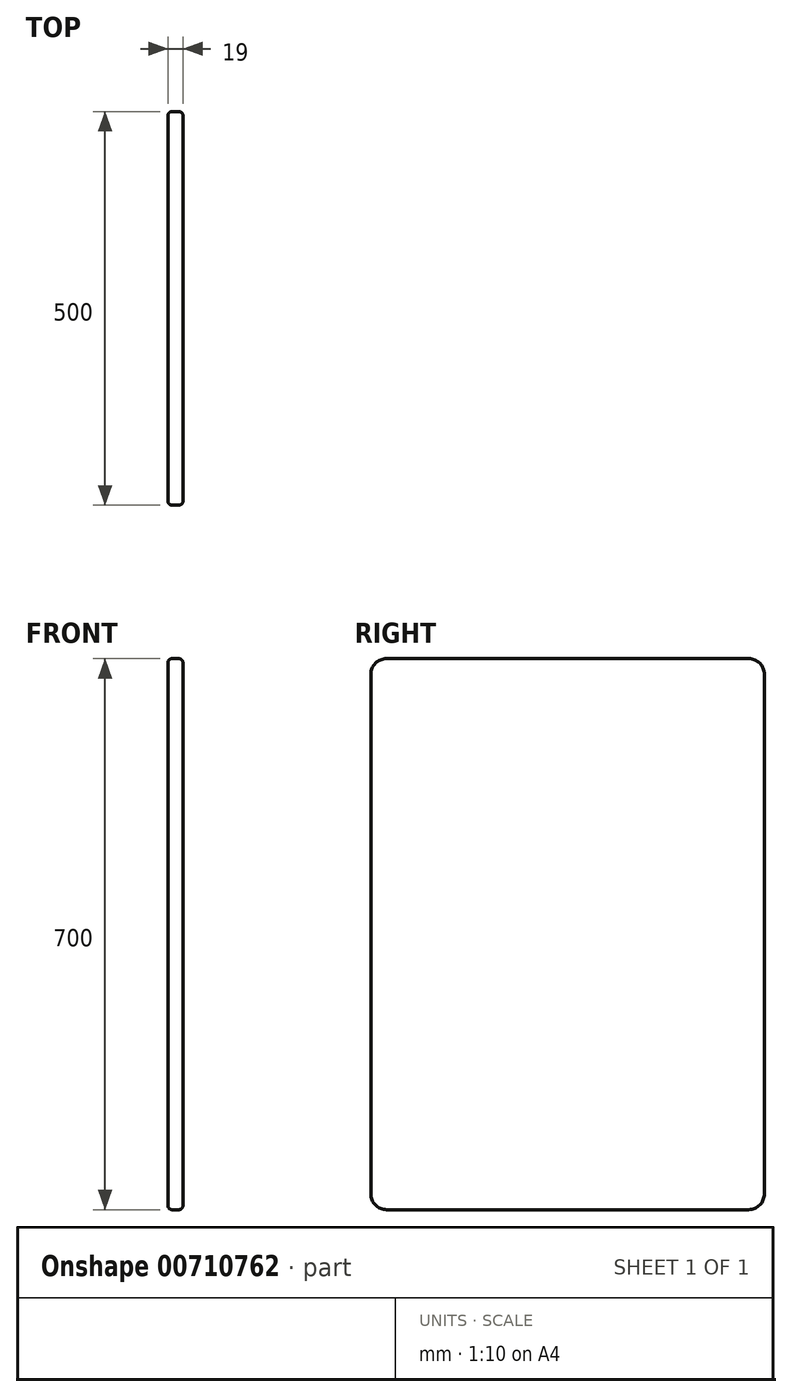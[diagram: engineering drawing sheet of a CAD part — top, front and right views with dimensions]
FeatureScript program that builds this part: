
annotation { "Feature Type Name" : "Feature", "Feature Type Description" : "" }
export const myFeature = defineFeature(function(context is Context, id is Id, definition is map)
    precondition{}
    {
        {
            var Q0;
            Q0=qCreatedBy(makeId("Right.planeOp"),FACE);
            var sketch = newSketch(context, id + "F0", { "sketchPlane" : qUnion([Q0])});
            skLineSegment(sketch, "E0.bottom", {"start": v(-33.4, 717.11) * mm, "end": v(466.6, 717.11) * mm});
            skLineSegment(sketch, "E0.top", {"start": v(-33.4, 17.11) * mm, "end": v(466.6, 17.11) * mm});
            skLineSegment(sketch, "E0.left", {"start": v(-33.4, 717.11) * mm, "end": v(-33.4, 17.11) * mm});
            skLineSegment(sketch, "E0.right", {"start": v(466.6, 717.11) * mm, "end": v(466.6, 17.11) * mm});
            skLineSegment(sketch, "E1", {"start": v(-33.4, 117.11) * mm, "end": v(466.6, 117.11) * mm, "construction": true});
            skLineSegment(sketch, "E2", {"start": v(-33.4, 367.11) * mm, "end": v(466.6, 367.11) * mm, "construction": true});
            skLineSegment(sketch, "E3", {"start": v(-33.4, 617.11) * mm, "end": v(466.6, 617.11) * mm, "construction": true});
            skSolve(sketch);
        }
        {
            var Q0;
            Q0=makeQuery(id+"F0.imprint","IMPRINT",FACE,{"disambiguationData":[TD([[makeQuery(id+"F0.imprint","IMPRINT",EDGE,{"derivedFrom":sQuery(id+"F0.wireOp",EDGE,"E0.bottom")}),-1.0]])]});
            extrude(context, id + "F1", {"entities" : qUnion([Q0]), "depth" : 19 * mm, "offsetDistance" : 25.4 * mm});
        }
        {
            var Q0;
            Q0=makeQuery(id+"F1.opExtrude","SWEPT_EDGE",EDGE,{"disambiguationData":[OSD([sQuery(id+"F0.wireOp",EDGE,"E0.bottom"),sQuery(id+"F0.wireOp",EDGE,"E0.left")])]});
            var Q1;
            Q1=makeQuery(id+"F1.opExtrude","SWEPT_EDGE",EDGE,{"disambiguationData":[OSD([sQuery(id+"F0.wireOp",EDGE,"E0.top"),sQuery(id+"F0.wireOp",EDGE,"E0.left")])]});
            var Q2;
            Q2=makeQuery(id+"F1.opExtrude","SWEPT_EDGE",EDGE,{"disambiguationData":[OSD([sQuery(id+"F0.wireOp",EDGE,"E0.top"),sQuery(id+"F0.wireOp",EDGE,"E0.right")])]});
            var Q3;
            Q3=makeQuery(id+"F1.opExtrude","SWEPT_EDGE",EDGE,{"disambiguationData":[OSD([sQuery(id+"F0.wireOp",EDGE,"E0.bottom"),sQuery(id+"F0.wireOp",EDGE,"E0.right")])]});
            fillet(context, id + "F2", {"entities" : qUnion([Q0, Q1, Q2, Q3]), "radius" : 20 * mm, "tangentPropagation" : true, "allowEdgeOverflow" : false});
        }
        {
            var Q0;
            Q0=makeQuery(id+"F1.opExtrude","CAP_EDGE",EDGE,{"disambiguationData":[OSD([sQuery(id+"F0.wireOp",EDGE,"E0.right")])],"isStart":true});
            var Q1;
            Q1=makeQuery(id+"F1.opExtrude","CAP_EDGE",EDGE,{"disambiguationData":[OSD([sQuery(id+"F0.wireOp",EDGE,"E0.right")])],"isStart":false});
            fillet(context, id + "F3", {"entities" : qUnion([Q0, Q1]), "radius" : 5 * mm, "tangentPropagation" : true, "allowEdgeOverflow" : false});
        }
    });
